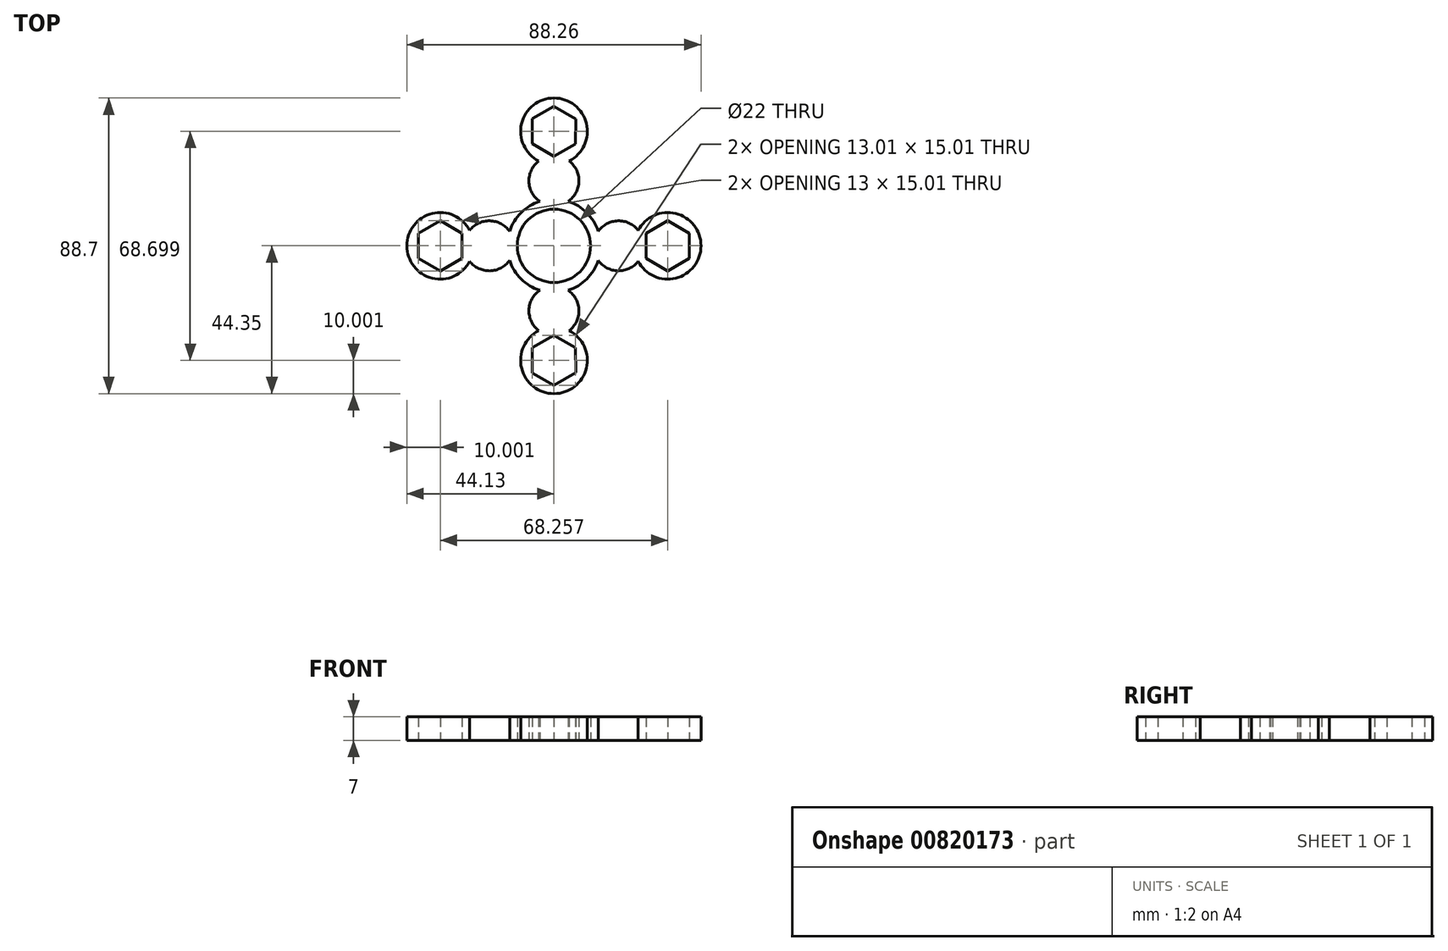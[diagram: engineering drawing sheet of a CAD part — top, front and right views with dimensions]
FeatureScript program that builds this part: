
annotation { "Feature Type Name" : "Feature", "Feature Type Description" : "" }
export const myFeature = defineFeature(function(context is Context, id is Id, definition is map)
    precondition{}
    {
        {
            var Q0;
            Q0=qCreatedBy(makeId("Top.planeOp"),FACE);
            var sketch = newSketch(context, id + "F0", { "sketchPlane" : qUnion([Q0])});
            skCircle(sketch, "E0", {"center": v(0, 0) * mm, "radius": 11 * mm});
            skCircle(sketch, "E1", {"center": v(0, 0) * mm, "radius": 14 * mm});
            skCircle(sketch, "E2", {"center": v(19.39, 0) * mm, "radius": 7.5 * mm});
            skCircle(sketch, "E3.MirrorC", {"center": v(-19.39, 0) * mm, "radius": 7.5 * mm});
            skCircle(sketch, "E4", {"center": v(0, 19.5) * mm, "radius": 7.5 * mm});
            skCircle(sketch, "E5.MirrorC", {"center": v(0, -19.5) * mm, "radius": 7.5 * mm});
            skCircle(sketch, "E6", {"center": v(34.13, 0) * mm, "radius": 10 * mm});
            skCircle(sketch, "E7", {"center": v(0, 34.35) * mm, "radius": 10 * mm});
            skCircle(sketch, "E8.MirrorC", {"center": v(0, -34.35) * mm, "radius": 10 * mm});
            skCircle(sketch, "E9.MirrorC", {"center": v(-34.13, 0) * mm, "radius": 10 * mm});
            skCircle(sketch, "E10.cCircle", {"center": v(34.13, 0) * mm, "radius": 6.5 * mm, "construction": true});
            skLineSegment(sketch, "E10.0", {"start": v(40.63, -3.75) * mm, "end": v(34.13, -7.5) * mm});
            skLineSegment(sketch, "E10.1", {"start": v(34.13, -7.5) * mm, "end": v(27.63, -3.75) * mm});
            skLineSegment(sketch, "E10.2", {"start": v(27.63, -3.75) * mm, "end": v(27.63, 3.75) * mm});
            skLineSegment(sketch, "E10.3", {"start": v(27.63, 3.75) * mm, "end": v(34.13, 7.5) * mm});
            skLineSegment(sketch, "E10.4", {"start": v(34.13, 7.5) * mm, "end": v(40.63, 3.75) * mm});
            skLineSegment(sketch, "E10.5", {"start": v(40.63, 3.75) * mm, "end": v(40.63, -3.75) * mm});
            skPoint(sketch, "E10.0.midPoint", {"position": v(37.38, -5.63) * mm});
            skCircle(sketch, "E11.cCircle", {"center": v(0, -34.35) * mm, "radius": 6.5 * mm, "construction": true});
            skLineSegment(sketch, "E11.0", {"start": v(6.5, -38.1) * mm, "end": v(0.01, -41.86) * mm});
            skLineSegment(sketch, "E11.1", {"start": v(0.01, -41.86) * mm, "end": v(-6.5, -38.11) * mm});
            skLineSegment(sketch, "E11.2", {"start": v(-6.5, -38.11) * mm, "end": v(-6.5, -30.6) * mm});
            skLineSegment(sketch, "E11.3", {"start": v(-6.5, -30.6) * mm, "end": v(-0.01, -26.84) * mm});
            skLineSegment(sketch, "E11.4", {"start": v(-0.01, -26.84) * mm, "end": v(6.5, -30.58) * mm});
            skLineSegment(sketch, "E11.5", {"start": v(6.5, -30.58) * mm, "end": v(6.5, -38.1) * mm});
            skPoint(sketch, "E11.0.midPoint", {"position": v(3.26, -39.97) * mm});
            skCircle(sketch, "E12.MirrorC", {"center": v(-34.13, 0) * mm, "radius": 6.5 * mm, "construction": true});
            skLineSegment(sketch, "E13.MirrorCS", {"start": v(-34.13, -7.5) * mm, "end": v(-27.63, -3.75) * mm});
            skLineSegment(sketch, "E14.MirrorCS", {"start": v(-27.63, -3.75) * mm, "end": v(-27.63, 3.75) * mm});
            skLineSegment(sketch, "E15.MirrorCS", {"start": v(-27.63, 3.75) * mm, "end": v(-34.13, 7.5) * mm});
            skLineSegment(sketch, "E16.MirrorCS", {"start": v(-34.13, 7.5) * mm, "end": v(-40.63, 3.75) * mm});
            skLineSegment(sketch, "E17.MirrorCS", {"start": v(-40.63, 3.75) * mm, "end": v(-40.63, -3.75) * mm});
            skLineSegment(sketch, "E18.MirrorCS", {"start": v(-40.63, -3.75) * mm, "end": v(-34.13, -7.5) * mm});
            skCircle(sketch, "E19.MirrorC", {"center": v(0, 34.35) * mm, "radius": 6.5 * mm, "construction": true});
            skLineSegment(sketch, "E20.MirrorCS", {"start": v(-0.01, 26.84) * mm, "end": v(6.5, 30.58) * mm});
            skLineSegment(sketch, "E21.MirrorCS", {"start": v(6.5, 30.58) * mm, "end": v(6.5, 38.1) * mm});
            skLineSegment(sketch, "E22.MirrorCS", {"start": v(6.5, 38.1) * mm, "end": v(0.01, 41.86) * mm});
            skLineSegment(sketch, "E23.MirrorCS", {"start": v(0.01, 41.86) * mm, "end": v(-6.5, 38.11) * mm});
            skLineSegment(sketch, "E24.MirrorCS", {"start": v(-6.5, 38.11) * mm, "end": v(-6.5, 30.6) * mm});
            skLineSegment(sketch, "E25.MirrorCS", {"start": v(-6.5, 30.6) * mm, "end": v(-0.01, 26.84) * mm});
            skSolve(sketch);
        }
        {
            var Q0;
            Q0 = qSketchRegion(id + "F0", true);
            extrude(context, id + "F1", {"entities" : qUnion([Q0]), "depth" : 7 * mm, "offsetDistance" : 25 * mm});
        }
    });
